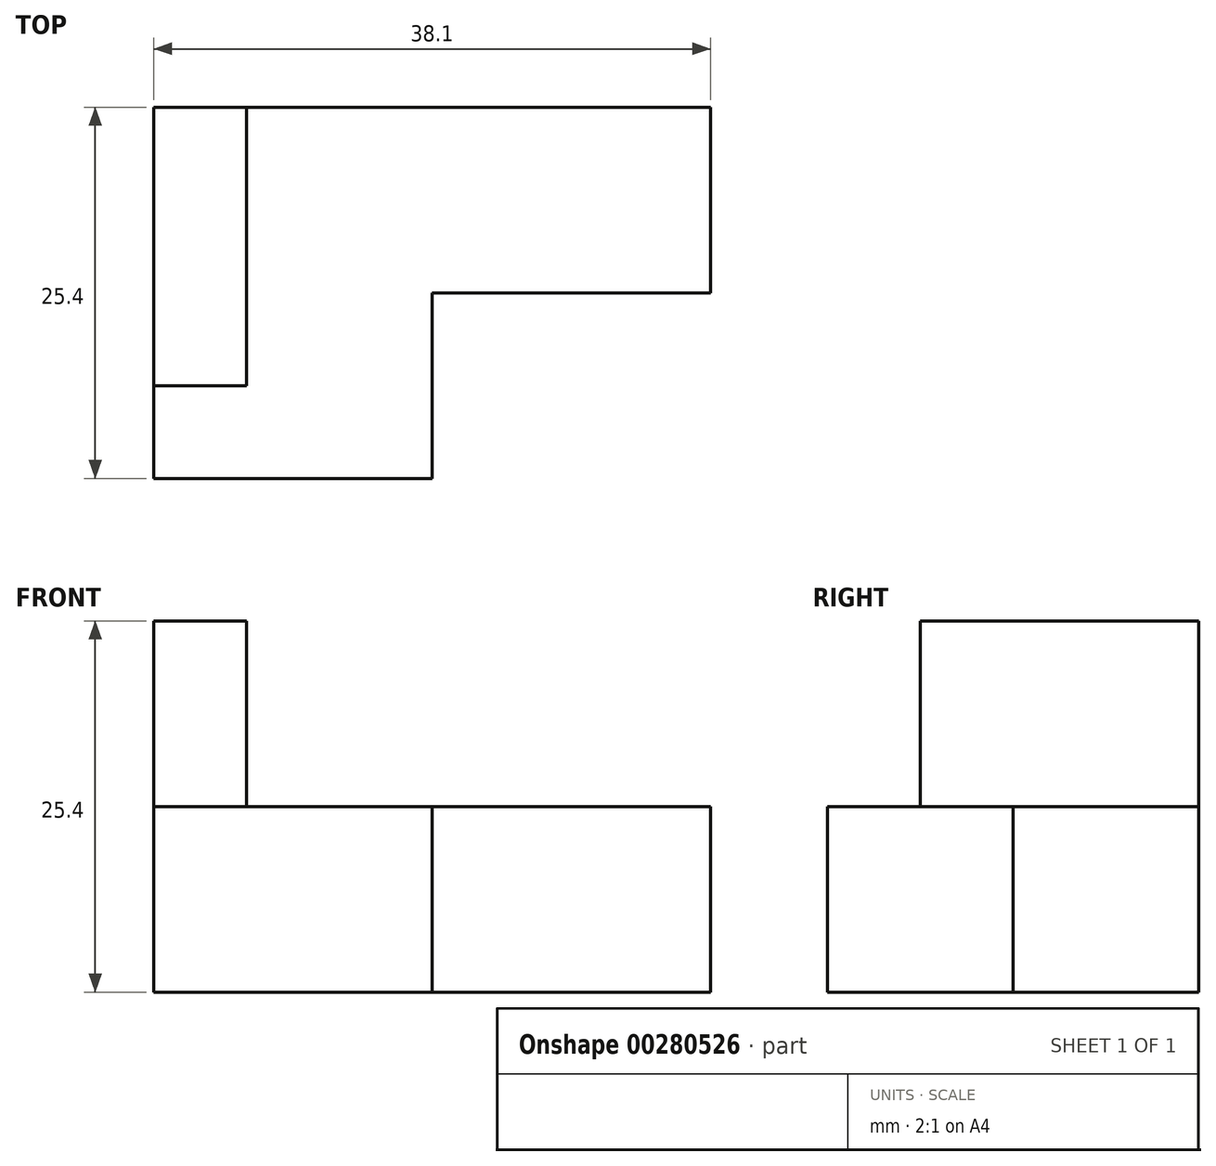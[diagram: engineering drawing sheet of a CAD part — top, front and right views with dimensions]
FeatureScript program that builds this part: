
annotation { "Feature Type Name" : "Feature", "Feature Type Description" : "" }
export const myFeature = defineFeature(function(context is Context, id is Id, definition is map)
    precondition{}
    {
        {
            var Q0;
            Q0=qCreatedBy(makeId("Front.planeOp"),FACE);
            var sketch = newSketch(context, id + "F0", { "sketchPlane" : qUnion([Q0])});
            skLineSegment(sketch, "E0", {"start": v(0, 0) * mm, "end": v(38.1, 0) * mm});
            skLineSegment(sketch, "E1", {"start": v(38.1, 0) * mm, "end": v(38.1, 12.7) * mm});
            skLineSegment(sketch, "E2", {"start": v(38.1, 12.7) * mm, "end": v(6.35, 12.7) * mm});
            skLineSegment(sketch, "E3", {"start": v(6.35, 12.7) * mm, "end": v(6.35, 25.4) * mm});
            skLineSegment(sketch, "E4", {"start": v(6.35, 25.4) * mm, "end": v(0, 25.4) * mm});
            skLineSegment(sketch, "E5", {"start": v(0, 25.4) * mm, "end": v(0, 0) * mm});
            skSolve(sketch);
        }
        {
            var Q0;
            Q0 = qSketchRegion(id + "F0", true);
            extrude(context, id + "F1", {"entities" : qUnion([Q0]), "depth" : 25.4 * mm});
        }
        {
            var Q0;
            Q0=makeQuery(id+"F1.opExtrude","CAP_FACE",FACE,{"disambiguationData":[OSD([sQuery(id+"F0.wireOp",EDGE,"E0"),sQuery(id+"F0.wireOp",EDGE,"E1"),sQuery(id+"F0.wireOp",EDGE,"E2"),sQuery(id+"F0.wireOp",EDGE,"E3"),sQuery(id+"F0.wireOp",EDGE,"E4"),sQuery(id+"F0.wireOp",EDGE,"E5")])],"isStart":false});
            var sketch = newSketch(context, id + "F2", { "sketchPlane" : qUnion([Q0])});
            skLineSegment(sketch, "E6.bottom", {"start": v(38.1, 0) * mm, "end": v(19.05, 0) * mm});
            skLineSegment(sketch, "E6.top", {"start": v(38.1, 12.7) * mm, "end": v(19.05, 12.7) * mm});
            skLineSegment(sketch, "E6.left", {"start": v(38.1, 0) * mm, "end": v(38.1, 12.7) * mm});
            skLineSegment(sketch, "E6.right", {"start": v(19.05, 0) * mm, "end": v(19.05, 12.7) * mm});
            skSolve(sketch);
        }
        {
            var Q0;
            Q0=makeQuery(id+"F2.imprint","IMPRINT",FACE,{"disambiguationData":[TD([[makeQuery(id+"F2.imprint","IMPRINT",EDGE,{"derivedFrom":sQuery(id+"F2.wireOp",EDGE,"E6.bottom")}),1.0]])]});
            extrude(context, id + "F3", {"entities" : qUnion([Q0]), "operationType" : NewBodyOperationType.REMOVE, "oppositeDirection" : true, "depth" : 12.7 * mm});
        }
        {
            var Q0;
            Q0=makeQuery(id+"F1.opExtrude","CAP_FACE",FACE,{"disambiguationData":[OSD([sQuery(id+"F0.wireOp",EDGE,"E0"),sQuery(id+"F0.wireOp",EDGE,"E1"),sQuery(id+"F0.wireOp",EDGE,"E2"),sQuery(id+"F0.wireOp",EDGE,"E3"),sQuery(id+"F0.wireOp",EDGE,"E4"),sQuery(id+"F0.wireOp",EDGE,"E5")])],"isStart":false});
            var sketch = newSketch(context, id + "F4", { "sketchPlane" : qUnion([Q0])});
            skLineSegment(sketch, "E7.bottom", {"start": v(6.35, 12.7) * mm, "end": v(0, 12.7) * mm});
            skLineSegment(sketch, "E7.top", {"start": v(6.35, 25.4) * mm, "end": v(0, 25.4) * mm});
            skLineSegment(sketch, "E7.left", {"start": v(6.35, 12.7) * mm, "end": v(6.35, 25.4) * mm});
            skLineSegment(sketch, "E7.right", {"start": v(0, 12.7) * mm, "end": v(0, 25.4) * mm});
            skSolve(sketch);
        }
        {
            var Q0;
            Q0=makeQuery(id+"F4.imprint","IMPRINT",FACE,{"disambiguationData":[TD([[makeQuery(id+"F4.imprint","IMPRINT",EDGE,{"derivedFrom":sQuery(id+"F4.wireOp",EDGE,"E7.bottom")}),-1.0]])]});
            extrude(context, id + "F5", {"entities" : qUnion([Q0]), "operationType" : NewBodyOperationType.REMOVE, "oppositeDirection" : true, "depth" : 6.35 * mm});
        }
    });
